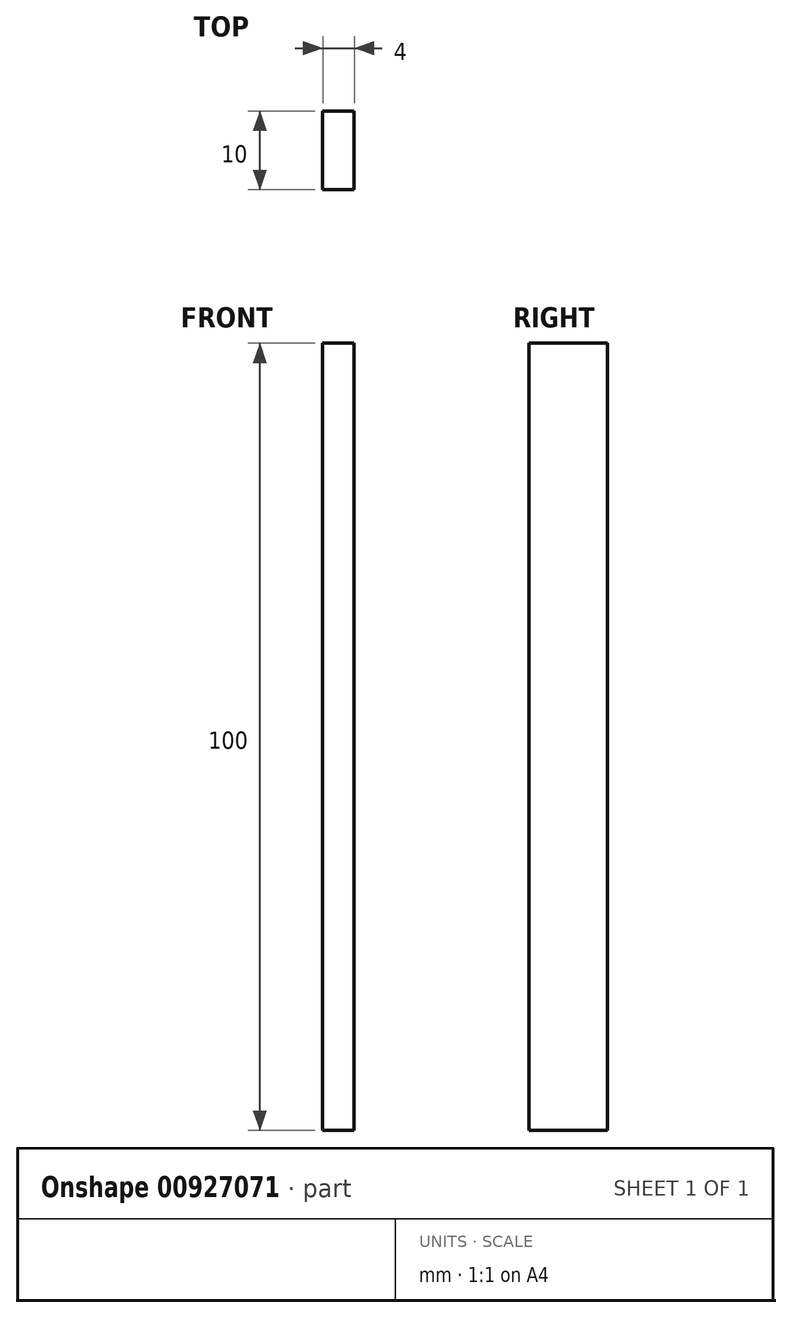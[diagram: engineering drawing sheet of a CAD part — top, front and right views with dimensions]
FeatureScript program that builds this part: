
annotation { "Feature Type Name" : "Feature", "Feature Type Description" : "" }
export const myFeature = defineFeature(function(context is Context, id is Id, definition is map)
    precondition{}
    {
        {
            var Q0;
            Q0=qCreatedBy(makeId("Front.planeOp"),FACE);
            var sketch = newSketch(context, id + "F0", { "sketchPlane" : qUnion([Q0])});
            skLineSegment(sketch, "E0.bottom", {"start": v(-106.47, 43.2) * mm, "end": v(-102.47, 43.2) * mm});
            skLineSegment(sketch, "E0.top", {"start": v(-106.47, -56.8) * mm, "end": v(-102.47, -56.8) * mm});
            skLineSegment(sketch, "E0.left", {"start": v(-106.47, 43.2) * mm, "end": v(-106.47, -56.8) * mm});
            skLineSegment(sketch, "E0.right", {"start": v(-102.47, 43.2) * mm, "end": v(-102.47, -56.8) * mm});
            skSolve(sketch);
        }
        {
            var Q0;
            Q0=makeQuery(id+"F0.imprint","IMPRINT",FACE,{"disambiguationData":[TD([[makeQuery(id+"F0.imprint","IMPRINT",EDGE,{"derivedFrom":sQuery(id+"F0.wireOp",EDGE,"E0.bottom")}),-1.0]])]});
            extrude(context, id + "F1", {"entities" : qUnion([Q0]), "depth" : 10 * mm, "offsetDistance" : 25 * mm});
        }
    });
